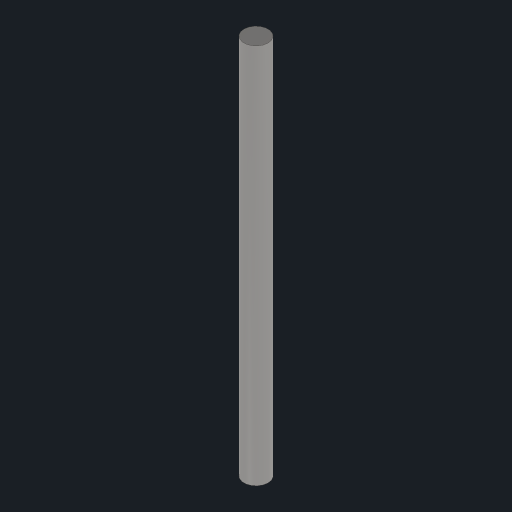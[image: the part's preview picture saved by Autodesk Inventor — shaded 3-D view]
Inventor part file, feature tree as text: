
AUTODESK INVENTOR PART (.ipt)
format: ipt  version: 2023.1 (Build 271208000, 208)  size: 74,752 bytes
history: native  units: mm
features: extrude x1, sketch x1
ambient origin geometry x8: Origin, YZ Plane, XZ Plane, XY Plane, X Axis, Y Axis, Z Axis, Center Point
bodies: Solid1 (feature_tree)
feature tree (2):
  extrude  "Extrusion1"  Depth=50.0mm TaperAngle=0.0deg
  sketch  "Sketch1"  dims[d0=3.175mm d1=50.0mm d2=0.0mm]
